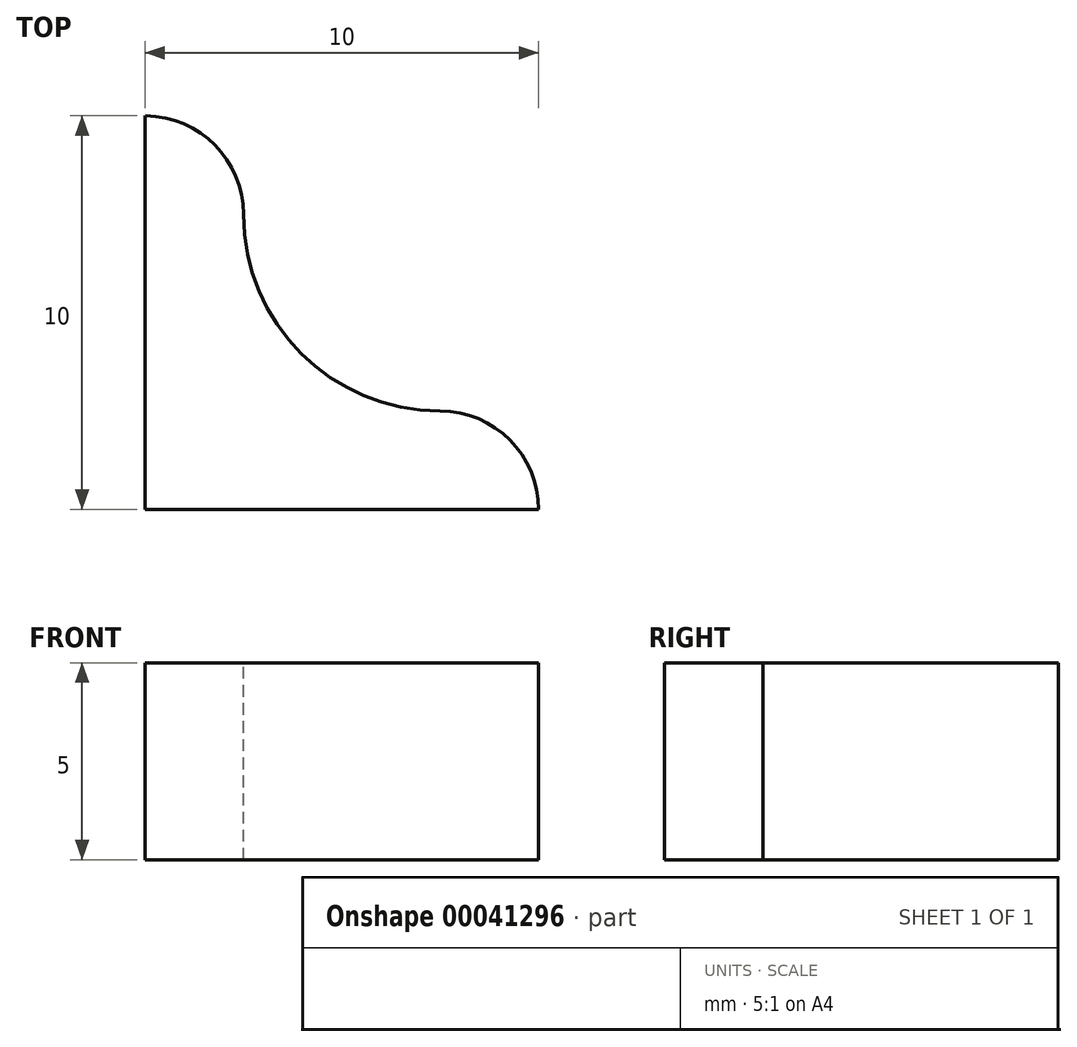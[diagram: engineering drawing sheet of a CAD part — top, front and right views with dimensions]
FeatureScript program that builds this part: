
annotation { "Feature Type Name" : "Feature", "Feature Type Description" : "" }
export const myFeature = defineFeature(function(context is Context, id is Id, definition is map)
    precondition{}
    {
        {
            var Q0;
            Q0=qCreatedBy(makeId("Top.planeOp"),FACE);
            var sketch = newSketch(context, id + "F0", { "sketchPlane" : qUnion([Q0])});
            skLineSegment(sketch, "E0", {"start": v(0, 0) * mm, "end": v(0, 10) * mm});
            skArc(sketch, "E1", {"start": v(2.5, 7.5) * mm, "mid": v(1.78, 9.26) * mm, "end": v(0.02, 10) * mm});
            skLineSegment(sketch, "E2", {"start": v(0, 7.5) * mm, "end": v(2.5, 7.5) * mm, "construction": true});
            skLineSegment(sketch, "E3", {"start": v(7.5, 0) * mm, "end": v(7.5, -13.16) * mm, "construction": true});
            skArc(sketch, "E4", {"start": v(2.5, 7.5) * mm, "mid": v(3.96, 3.96) * mm, "end": v(7.5, 2.5) * mm});
            skLineSegment(sketch, "E5", {"start": v(0, 5.04) * mm, "end": v(0, 5.04) * mm});
            skArc(sketch, "E6", {"start": v(10, 0) * mm, "mid": v(9.27, 1.77) * mm, "end": v(7.5, 2.5) * mm});
            skLineSegment(sketch, "E7", {"start": v(0, 0) * mm, "end": v(10, 0) * mm});
            skSolve(sketch);
        }
        {
            var Q0;
            Q0=sQuery(id+"F0.wireOp",EDGE,"E7");
            var Q1;
            Q1=sQuery(id+"F0.wireOp",EDGE,"E0");
            var Q2;
            Q2=sQuery(id+"F0.wireOp",EDGE,"E6");
            var Q3;
            Q3=sQuery(id+"F0.wireOp",EDGE,"E4");
            var Q4;
            Q4=sQuery(id+"F0.wireOp",EDGE,"E1");
            extrude(context, id + "F1", {"bodyType" : ToolBodyType.SURFACE, "surfaceEntities" : qUnion([Q0, Q1, Q2, Q3, Q4]), "depth" : 5 * mm});
        }
    });
